# Revit family: PRESTO_75145_MODULMIX_HOSPITAL_TAP_EN
name_source: partatom
category: Generic Models
revit_build: Autodesk Revit 2015 (Build: 20140903_1530(x64)
units: mm (PartAtom-declared; Revit-internal decimal feet)

## types (1)
- Default
    BIMobject category = Taps & Mixers
    BOSUseNativeGeometries = 1
    Design country = France
    Edition number = 1
    IFC Classification = Sanitary Terminal
    Manufacturer country = France
    Manufacturer name = Presto
    Material main = Brass
    Material secondary = Chrome
    Nominal height = 0
    Nominal width = 0
    Presto_BOPCEditionNumber = 1
    Presto_CW_inlet = G'3/8
    Presto_flow = Débit ajustable entre 5 et 26L/min
    Presto_material = laiton
    Presto_operating_pressure = 1 à 5 bar - Pression recommandée : 3 bar
    Presto_outlet = M24X1
    Presto_secondary_material = SPEX
    Presto_warranty = 10
    Product Guid = eef5c20a-4f16-4e0b-9eeb-e2fe43dba128
    Product SKU = 75145
    Product data url = https://bimobject.com
    QR code = http://bimobject.com
    UNSPSC Code = 301815
    Weight Net (Kg) = 0

## geometry (parser evidence)
native form markers: Sweep x3
no freeform markers — native parametric forms only
